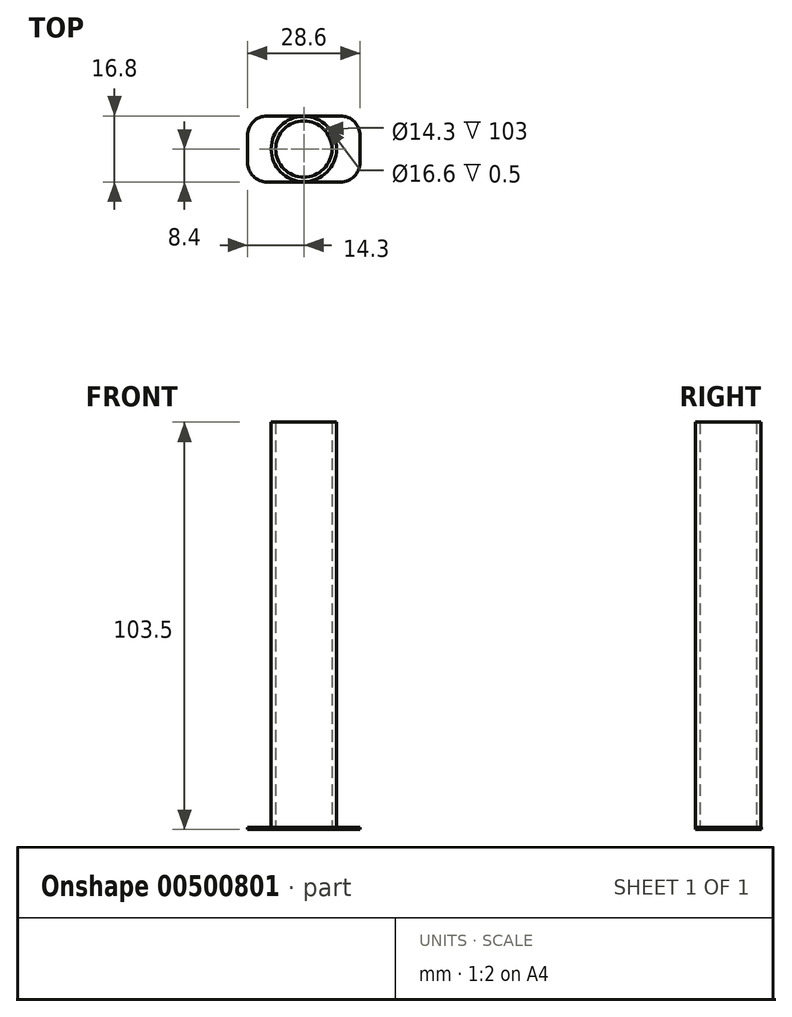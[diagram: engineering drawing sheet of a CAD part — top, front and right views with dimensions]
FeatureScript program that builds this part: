
annotation { "Feature Type Name" : "Feature", "Feature Type Description" : "" }
export const myFeature = defineFeature(function(context is Context, id is Id, definition is map)
    precondition{}
    {
        {
            var Q0;
            Q0=qCreatedBy(makeId("Top.planeOp"),FACE);
            var sketch = newSketch(context, id + "F0", { "sketchPlane" : qUnion([Q0])});
            skCircle(sketch, "E0", {"center": v(0, 0) * mm, "radius": 7.15 * mm});
            skCircle(sketch, "E1", {"center": v(0, 0) * mm, "radius": 8.3 * mm});
            skLineSegment(sketch, "E2.bottom", {"start": v(14.3, -8.4) * mm, "end": v(-14.3, -8.4) * mm});
            skLineSegment(sketch, "E2.top", {"start": v(14.3, 8.4) * mm, "end": v(-14.3, 8.4) * mm});
            skLineSegment(sketch, "E2.left", {"start": v(14.3, -8.4) * mm, "end": v(14.3, 8.4) * mm});
            skLineSegment(sketch, "E2.right", {"start": v(-14.3, -8.4) * mm, "end": v(-14.3, 8.4) * mm});
            skLineSegment(sketch, "E3", {"start": v(8.3, 0) * mm, "end": v(14.3, 0) * mm});
            skLineSegment(sketch, "E4", {"start": v(-8.3, 0) * mm, "end": v(-14.3, 0) * mm});
            skCircle(sketch, "E5", {"center": v(0, 0) * mm, "radius": 2.5 * mm});
            skCircle(sketch, "E6", {"center": v(0, 0) * mm, "radius": 1.23 * mm});
            skCircle(sketch, "E7", {"center": v(0, 0) * mm, "radius": 0.75 * mm});
            skSolve(sketch);
        }
        {
            var Q0;
            {var subQ1=sQuery(id+"F0.wireOp",EDGE,"E2.bottom");Q0=makeQuery(id+"F0.imprint","IMPRINT",FACE,{"disambiguationData":[TD([[makeQuery(id+"F0.imprint","IMPRINT",EDGE,{"derivedFrom":subQ1}),-1.0]])]});}
            var Q1;
            {var subQ1=sQuery(id+"F0.wireOp",EDGE,"E2.top");Q1=makeQuery(id+"F0.imprint","IMPRINT",FACE,{"disambiguationData":[TD([[makeQuery(id+"F0.imprint","IMPRINT",EDGE,{"derivedFrom":subQ1}),1.0]])]});}
            extrude(context, id + "F1", {"entities" : qUnion([Q0, Q1]), "oppositeDirection" : true, "depth" : .5 * mm, "offsetDistance" : 25 * mm});
        }
        {
            var Q0;
            Q0=makeQuery(id+"F0.imprint","IMPRINT",FACE,{"disambiguationData":[TD([[makeQuery(id+"F0.imprint","IMPRINT",EDGE,{"derivedFrom":sQuery(id+"F0.wireOp",EDGE,"E0")}),-1.0]])]});
            extrude(context, id + "F2", {"entities" : qUnion([Q0]), "depth" : 100 * mm, "offsetDistance" : 25 * mm});
        }
        {
            var Q0;
            Q0=makeQuery(id+"F1.opExtrude","SWEPT_EDGE",EDGE,{"disambiguationData":[OSD([sQuery(id+"F0.wireOp",EDGE,"E2.bottom"),sQuery(id+"F0.wireOp",EDGE,"E2.left")])]});
            var Q1;
            Q1=makeQuery(id+"F1.opExtrude","SWEPT_EDGE",EDGE,{"disambiguationData":[OSD([sQuery(id+"F0.wireOp",EDGE,"E2.top"),sQuery(id+"F0.wireOp",EDGE,"E2.left")])]});
            var Q2;
            Q2=makeQuery(id+"F1.opExtrude","SWEPT_EDGE",EDGE,{"disambiguationData":[OSD([sQuery(id+"F0.wireOp",EDGE,"E2.top"),sQuery(id+"F0.wireOp",EDGE,"E2.right")])]});
            var Q3;
            Q3=makeQuery(id+"F1.opExtrude","SWEPT_EDGE",EDGE,{"disambiguationData":[OSD([sQuery(id+"F0.wireOp",EDGE,"E2.bottom"),sQuery(id+"F0.wireOp",EDGE,"E2.right")])]});
            fillet(context, id + "F3", {"entities" : qUnion([Q0, Q1, Q2, Q3]), "radius" : 5 * mm, "tangentPropagation" : true, "allowEdgeOverflow" : false});
        }
        {
            var Q0;
            Q0=makeQuery(id+"F0.imprint","IMPRINT",FACE,{"disambiguationData":[TD([[makeQuery(id+"F0.imprint","IMPRINT",EDGE,{"derivedFrom":sQuery(id+"F0.wireOp",EDGE,"E0")}),-1.0]])]});
            var Q1;
            Q1=sQuery(id+"F0.wireOp",EDGE,"E0");
            extrude(context, id + "F4", {"entities" : qUnion([Q0]), "operationType" : NewBodyOperationType.ADD, "surfaceEntities" : qUnion([Q1]), "depth" : 103 * mm, "offsetDistance" : 25 * mm});
        }
    });
